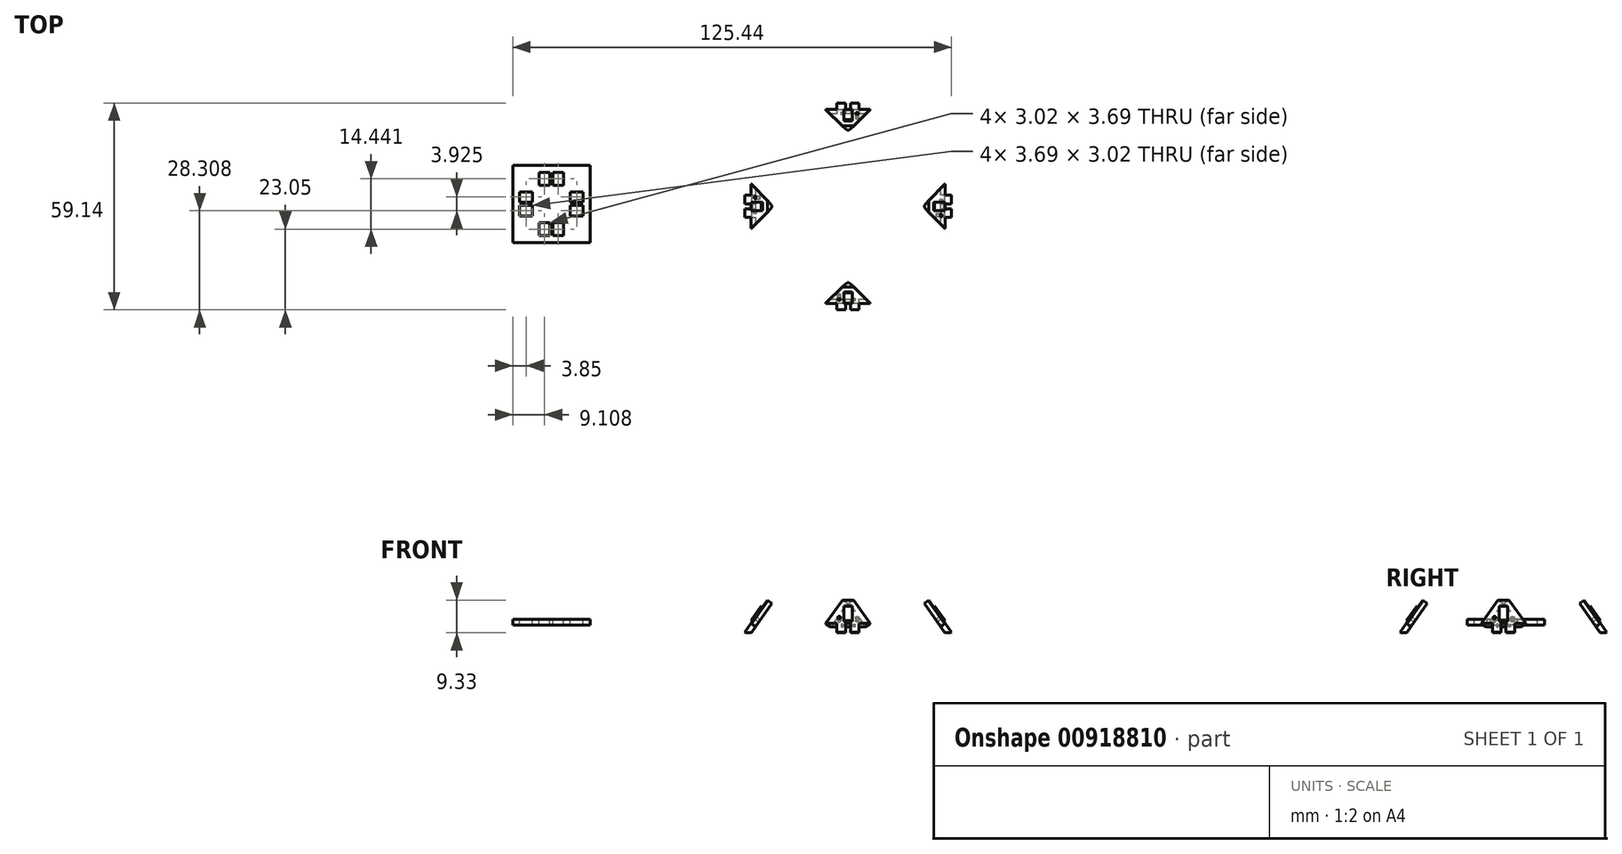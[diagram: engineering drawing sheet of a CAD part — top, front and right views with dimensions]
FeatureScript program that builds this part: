
annotation { "Feature Type Name" : "Feature", "Feature Type Description" : "" }
export const myFeature = defineFeature(function(context is Context, id is Id, definition is map)
    precondition{}
    {
        {
            var Q0;
            Q0=qCreatedBy(makeId("Top.planeOp"),FACE);
            var sketch = newSketch(context, id + "F0", { "sketchPlane" : qUnion([Q0])});
            skLineSegment(sketch, "E0", {"start": v(0, 0) * mm, "end": v(0, 27.35) * mm});
            skLineSegment(sketch, "E1", {"start": v(0, 0) * mm, "end": v(10, 0) * mm});
            skLineSegment(sketch, "E2", {"start": v(10, 0) * mm, "end": v(10, -10) * mm});
            skLineSegment(sketch, "E3", {"start": v(10, -10) * mm, "end": v(0, 0) * mm});
            skLineSegment(sketch, "E4", {"start": v(-60.25, -8.37) * mm, "end": v(-60.25, -4.67) * mm});
            skLineSegment(sketch, "E5", {"start": v(-63.27, -8.37) * mm, "end": v(-63.27, -4.97) * mm});
            skLineSegment(sketch, "E6", {"start": v(-63.27, -4.97) * mm, "end": v(-63.27, -4.67) * mm});
            skLineSegment(sketch, "E7", {"start": v(-63.27, -4.67) * mm, "end": v(-60.25, -4.67) * mm});
            skLineSegment(sketch, "E8", {"start": v(-63.27, -8.37) * mm, "end": v(-60.25, -8.37) * mm});
            skLineSegment(sketch, "E9", {"start": v(-63.27, -8.37) * mm, "end": v(-63.27, -8.07) * mm});
            skLineSegment(sketch, "E10", {"start": v(-59.35, -8.37) * mm, "end": v(-59.35, -4.67) * mm});
            skLineSegment(sketch, "E11", {"start": v(-56.33, -8.37) * mm, "end": v(-56.33, -4.97) * mm});
            skLineSegment(sketch, "E12", {"start": v(-56.33, -4.97) * mm, "end": v(-56.33, -4.67) * mm});
            skLineSegment(sketch, "E13", {"start": v(-56.33, -4.67) * mm, "end": v(-59.35, -4.67) * mm});
            skLineSegment(sketch, "E14", {"start": v(-56.33, -8.37) * mm, "end": v(-59.35, -8.37) * mm});
            skLineSegment(sketch, "E15", {"start": v(-56.33, -8.37) * mm, "end": v(-56.33, -8.07) * mm});
            skLineSegment(sketch, "E16", {"start": v(-50.73, 1.15) * mm, "end": v(-54.43, 1.15) * mm});
            skLineSegment(sketch, "E17", {"start": v(-50.73, 4.17) * mm, "end": v(-54.13, 4.17) * mm});
            skLineSegment(sketch, "E18", {"start": v(-54.13, 4.17) * mm, "end": v(-54.43, 4.17) * mm});
            skLineSegment(sketch, "E19", {"start": v(-54.43, 4.17) * mm, "end": v(-54.43, 1.15) * mm});
            skLineSegment(sketch, "E20", {"start": v(-50.73, 4.17) * mm, "end": v(-50.73, 1.15) * mm});
            skLineSegment(sketch, "E21", {"start": v(-50.73, 4.17) * mm, "end": v(-51.03, 4.17) * mm});
            skLineSegment(sketch, "E22", {"start": v(-50.73, 0.25) * mm, "end": v(-54.43, 0.25) * mm});
            skLineSegment(sketch, "E23", {"start": v(-50.73, -2.77) * mm, "end": v(-54.13, -2.77) * mm});
            skLineSegment(sketch, "E24", {"start": v(-54.13, -2.77) * mm, "end": v(-54.43, -2.77) * mm});
            skLineSegment(sketch, "E25", {"start": v(-54.43, -2.77) * mm, "end": v(-54.43, 0.25) * mm});
            skLineSegment(sketch, "E26", {"start": v(-50.73, -2.77) * mm, "end": v(-50.73, 0.25) * mm});
            skLineSegment(sketch, "E27", {"start": v(-50.73, -2.77) * mm, "end": v(-51.03, -2.77) * mm});
            skLineSegment(sketch, "E28", {"start": v(-60.25, 9.77) * mm, "end": v(-60.25, 6.07) * mm});
            skLineSegment(sketch, "E29", {"start": v(-63.27, 9.77) * mm, "end": v(-63.27, 6.37) * mm});
            skLineSegment(sketch, "E30", {"start": v(-63.27, 6.37) * mm, "end": v(-63.27, 6.07) * mm});
            skLineSegment(sketch, "E31", {"start": v(-63.27, 6.07) * mm, "end": v(-60.25, 6.07) * mm});
            skLineSegment(sketch, "E32", {"start": v(-63.27, 9.77) * mm, "end": v(-60.25, 9.77) * mm});
            skLineSegment(sketch, "E33", {"start": v(-63.27, 9.77) * mm, "end": v(-63.27, 9.47) * mm});
            skLineSegment(sketch, "E34", {"start": v(-59.35, 9.77) * mm, "end": v(-59.35, 6.07) * mm});
            skLineSegment(sketch, "E35", {"start": v(-56.33, 9.77) * mm, "end": v(-56.33, 6.37) * mm});
            skLineSegment(sketch, "E36", {"start": v(-56.33, 6.37) * mm, "end": v(-56.33, 6.07) * mm});
            skLineSegment(sketch, "E37", {"start": v(-56.33, 6.07) * mm, "end": v(-59.35, 6.07) * mm});
            skLineSegment(sketch, "E38", {"start": v(-56.33, 9.77) * mm, "end": v(-59.35, 9.77) * mm});
            skLineSegment(sketch, "E39", {"start": v(-56.33, 9.77) * mm, "end": v(-56.33, 9.47) * mm});
            skLineSegment(sketch, "E40", {"start": v(-68.87, 1.15) * mm, "end": v(-65.17, 1.15) * mm});
            skLineSegment(sketch, "E41", {"start": v(-68.87, 4.17) * mm, "end": v(-65.47, 4.17) * mm});
            skLineSegment(sketch, "E42", {"start": v(-65.47, 4.17) * mm, "end": v(-65.17, 4.17) * mm});
            skLineSegment(sketch, "E43", {"start": v(-65.17, 4.17) * mm, "end": v(-65.17, 1.15) * mm});
            skLineSegment(sketch, "E44", {"start": v(-68.87, 4.17) * mm, "end": v(-68.87, 1.15) * mm});
            skLineSegment(sketch, "E45", {"start": v(-68.87, 4.17) * mm, "end": v(-68.57, 4.17) * mm});
            skLineSegment(sketch, "E46", {"start": v(-68.87, 0.25) * mm, "end": v(-65.17, 0.25) * mm});
            skLineSegment(sketch, "E47", {"start": v(-68.87, -2.77) * mm, "end": v(-65.47, -2.77) * mm});
            skLineSegment(sketch, "E48", {"start": v(-65.47, -2.77) * mm, "end": v(-65.17, -2.77) * mm});
            skLineSegment(sketch, "E49", {"start": v(-65.17, -2.77) * mm, "end": v(-65.17, 0.25) * mm});
            skLineSegment(sketch, "E50", {"start": v(-68.87, -2.77) * mm, "end": v(-68.87, 0.25) * mm});
            skLineSegment(sketch, "E51", {"start": v(-68.87, -2.77) * mm, "end": v(-68.57, -2.77) * mm});
            skLineSegment(sketch, "E52", {"start": v(-48.73, 0.7) * mm, "end": v(-48.73, -10.37) * mm});
            skLineSegment(sketch, "E53", {"start": v(-48.73, -10.37) * mm, "end": v(-59.8, -10.37) * mm});
            skLineSegment(sketch, "E54", {"start": v(-70.87, 0.7) * mm, "end": v(-70.87, -10.37) * mm});
            skLineSegment(sketch, "E55", {"start": v(-70.87, -10.37) * mm, "end": v(-59.8, -10.37) * mm});
            skLineSegment(sketch, "E56", {"start": v(-48.73, 0.7) * mm, "end": v(-48.73, 11.77) * mm});
            skLineSegment(sketch, "E57", {"start": v(-48.73, 11.77) * mm, "end": v(-59.8, 11.77) * mm});
            skLineSegment(sketch, "E58", {"start": v(-70.87, 0.7) * mm, "end": v(-70.87, 11.77) * mm});
            skLineSegment(sketch, "E59", {"start": v(-70.87, 11.77) * mm, "end": v(-59.8, 11.77) * mm});
            skSolve(sketch);
        }
        {
            var Q0;
            Q0=sQuery(id+"F0.wireOp",EDGE,"E0");
            cPlane(context, id + "F1", {"entities" : qUnion([Q0]), "cplaneType" : CPlaneType.LINE_ANGLE, "offset" : 25 * mm, "angle" : 54.74 * degree, "oppositeDirection" : true, "width" : 150 * mm, "height" : 150 * mm});
        }
        {
            var Q0;
            Q0=qCreatedBy(id+"F1.planeOp",FACE);
            var sketch = newSketch(context, id + "F2", { "sketchPlane" : qUnion([Q0])});
            skLineSegment(sketch, "E60", {"start": v(6.35, -2.55) * mm, "end": v(1.62, 5.64) * mm});
            skLineSegment(sketch, "E61", {"start": v(-1.62, 5.64) * mm, "end": v(-6.35, -2.55) * mm});
            skLineSegment(sketch, "E62", {"start": v(3.18, -5.64) * mm, "end": v(0.75, -5.64) * mm});
            skLineSegment(sketch, "E63", {"start": v(-0.75, -5.64) * mm, "end": v(-3.18, -5.64) * mm});
            skLineSegment(sketch, "E64", {"start": v(1.62, 5.64) * mm, "end": v(-1.62, 5.64) * mm});
            skLineSegment(sketch, "E65", {"start": v(-3.18, -5.64) * mm, "end": v(-3.18, -2.55) * mm});
            skLineSegment(sketch, "E66", {"start": v(3.18, -5.64) * mm, "end": v(3.18, -2.55) * mm});
            skLineSegment(sketch, "E67", {"start": v(-6.35, -2.55) * mm, "end": v(-3.18, -2.55) * mm});
            skLineSegment(sketch, "E68", {"start": v(3.18, -2.55) * mm, "end": v(6.35, -2.55) * mm});
            skLineSegment(sketch, "E69", {"start": v(-0.75, -5.64) * mm, "end": v(-0.75, -2.55) * mm});
            skCircle(sketch, "E70", {"center": v(-2.55, -0.48) * mm, "radius": 0.42 * mm});
            skLineSegment(sketch, "E71", {"start": v(-0.75, -2.55) * mm, "end": v(0.75, -2.55) * mm});
            skLineSegment(sketch, "E72", {"start": v(0.75, -2.55) * mm, "end": v(0.75, -5.64) * mm});
            skLineSegment(sketch, "E73", {"start": v(1.96, -2.55) * mm, "end": v(1.46, -2.55) * mm});
            skLineSegment(sketch, "E74", {"start": v(1.46, -2.55) * mm, "end": v(1.46, -2.05) * mm});
            skLineSegment(sketch, "E75", {"start": v(1.46, -2.05) * mm, "end": v(1.96, -2.05) * mm});
            skLineSegment(sketch, "E76", {"start": v(1.96, -2.05) * mm, "end": v(1.96, -2.55) * mm});
            skSolve(sketch);
        }
        {
            var Q0;
            Q0=qSketchRegion(id+"F2",true);
            var Q1;
            Q1=makeQuery(id+"F2.imprint","IMPRINT",FACE,{"disambiguationData":[TD([[makeQuery(id+"F2.imprint","IMPRINT",EDGE,{"derivedFrom":sQuery(id+"F2.wireOp",EDGE,"E73")}),-1.0]])]});
            extrude(context, id + "F3", {"entities" : qUnion([Q0, Q1]), "depth" : 1.6 * mm, "offsetDistance" : 25 * mm});
        }
        {
            var Q0;
            Q0=makeQuery(id+"F2.imprint","IMPRINT",FACE,{"disambiguationData":[TD([[makeQuery(id+"F2.imprint","IMPRINT",EDGE,{"derivedFrom":sQuery(id+"F2.wireOp",EDGE,"E73")}),-1.0]])]});
            extrude(context, id + "F4", {"entities" : qUnion([Q0]), "operationType" : NewBodyOperationType.REMOVE, "depth" : .6 * mm, "offsetDistance" : 25 * mm});
        }
        {
            var Q0;
            Q0=qCreatedBy(makeId("Right.planeOp"),FACE);
            cPlane(context, id + "F5", {"entities" : qUnion([Q0]), "cplaneType" : CPlaneType.OFFSET, "offset" : 25 * mm, "width" : 150 * mm, "height" : 150 * mm});
        }
        {
            var Q0;
            Q0=qCreatedBy(id+"F5.planeOp",FACE);
            var sketch = newSketch(context, id + "F6", { "sketchPlane" : qUnion([Q0])});
            skLineSegment(sketch, "E77", {"start": v(0, 0) * mm, "end": v(0, 26.14) * mm});
            skSolve(sketch);
        }
        {
            var Q0;
            Q0=qCreatedBy(makeId("Front.planeOp"),FACE);
            var sketch = newSketch(context, id + "F7", { "sketchPlane" : qUnion([Q0])});
            skPoint(sketch, "E78.0", {"position": v(-4.57, -3.69) * mm});
            skPoint(sketch, "E78.1", {"position": v(-3.26, -4.6) * mm});
            skPoint(sketch, "E78.2", {"position": v(-2.37, -3.35) * mm});
            skLineSegment(sketch, "E79", {"start": v(-3.26, -4.6) * mm, "end": v(-4.57, -3.69) * mm});
            skLineSegment(sketch, "E80", {"start": v(-4.57, -3.69) * mm, "end": v(-4.4, -3.8) * mm});
            skLineSegment(sketch, "E81", {"start": v(-3.26, -4.6) * mm, "end": v(-2.62, -3.71) * mm});
            skLineSegment(sketch, "E82", {"start": v(-2.62, -3.71) * mm, "end": v(-4.4, -3.8) * mm});
            skSolve(sketch);
        }
        {
            var Q0;
            Q0=makeQuery(id+"F7.imprint","IMPRINT",FACE,{"disambiguationData":[TD([[makeQuery(id+"F7.imprint","IMPRINT",EDGE,{"derivedFrom":sQuery(id+"F7.wireOp",EDGE,"E79")}),-1.0]])]});
            extrude(context, id + "F8", {"entities" : qUnion([Q0]), "operationType" : NewBodyOperationType.REMOVE, "endBound" : BoundingType.SYMMETRIC, "oppositeDirection" : true, "depth" : 25 * mm, "offsetDistance" : 25 * mm});
        }
        {
            var Q0;
            Q0=makeQuery(id+"F3.opExtrude","SWEPT_FACE",FACE,{"disambiguationData":[OSD([sQuery(id+"F2.wireOp",EDGE,"E64")])]});
            var sketch = newSketch(context, id + "F9", { "sketchPlane" : qUnion([Q0])});
            skPoint(sketch, "E83.0", {"position": v(0, -1.62) * mm});
            skPoint(sketch, "E83.1", {"position": v(-1.6, -1.62) * mm});
            skPoint(sketch, "E83.2", {"position": v(0, 1.62) * mm});
            skPoint(sketch, "E83.3", {"position": v(-1.6, 1.62) * mm});
            skLineSegment(sketch, "E84", {"start": v(0, -1.62) * mm, "end": v(0, -0.22) * mm});
            skLineSegment(sketch, "E85", {"start": v(0, -1.62) * mm, "end": v(-1.4, -1.62) * mm});
            skLineSegment(sketch, "E86", {"start": v(0, 1.62) * mm, "end": v(0, 0.22) * mm});
            skLineSegment(sketch, "E87", {"start": v(0, 1.62) * mm, "end": v(-1.4, 1.62) * mm});
            skLineSegment(sketch, "E88", {"start": v(-1.4, 1.62) * mm, "end": v(0, 0.22) * mm});
            skLineSegment(sketch, "E89", {"start": v(0, -0.22) * mm, "end": v(-1.4, -1.62) * mm});
            skSolve(sketch);
        }
        {
            var Q0;
            Q0=makeQuery(id+"F9.imprint","IMPRINT",FACE,{"disambiguationData":[TD([[makeQuery(id+"F9.imprint","IMPRINT",EDGE,{"derivedFrom":sQuery(id+"F9.wireOp",EDGE,"E86")}),1.0]])]});
            var Q1;
            Q1=sQuery(id+"F2.wireOp",EDGE,"E61");
            sweep(context, id + "F10", {"operationType" : NewBodyOperationType.REMOVE, "profiles" : qUnion([Q0]), "path" : qUnion([Q1])});
        }
        {
            var Q0;
            Q0=makeQuery(id+"F9.imprint","IMPRINT",FACE,{"disambiguationData":[TD([[makeQuery(id+"F9.imprint","IMPRINT",EDGE,{"derivedFrom":sQuery(id+"F9.wireOp",EDGE,"E84")}),1.0]])]});
            var Q1;
            Q1=sQuery(id+"F2.wireOp",EDGE,"E60");
            sweep(context, id + "F11", {"operationType" : NewBodyOperationType.REMOVE, "profiles" : qUnion([Q0]), "path" : qUnion([Q1])});
        }
        {
            var Q0;
            Q0=makeQuery(id+"F3.opExtrude","CAP_FACE",FACE,{"disambiguationData":[OSD([sQuery(id+"F2.wireOp",EDGE,"E60"),sQuery(id+"F2.wireOp",EDGE,"E61"),sQuery(id+"F2.wireOp",EDGE,"E62"),sQuery(id+"F2.wireOp",EDGE,"E63"),sQuery(id+"F2.wireOp",EDGE,"E64"),sQuery(id+"F2.wireOp",EDGE,"E65"),sQuery(id+"F2.wireOp",EDGE,"E66"),sQuery(id+"F2.wireOp",EDGE,"E67"),sQuery(id+"F2.wireOp",EDGE,"E68"),sQuery(id+"F2.wireOp",EDGE,"E69"),sQuery(id+"F2.wireOp",EDGE,"E70"),sQuery(id+"F2.wireOp",EDGE,"E71"),sQuery(id+"F2.wireOp",EDGE,"E72")])],"isStart":false});
            var sketch = newSketch(context, id + "F12", { "sketchPlane" : qUnion([Q0])});
            skPoint(sketch, "E90.0", {"position": v(0, -2.55) * mm});
            skLineSegment(sketch, "E91", {"start": v(0, -2.55) * mm, "end": v(0, -2.55) * mm});
            skLineSegment(sketch, "E92", {"start": v(0, -2.55) * mm, "end": v(0, -1.86) * mm});
            skLineSegment(sketch, "E93", {"start": v(0, -1.86) * mm, "end": v(1.25, -1.86) * mm});
            skLineSegment(sketch, "E94", {"start": v(1.25, -1.86) * mm, "end": v(1.25, 3.24) * mm});
            skLineSegment(sketch, "E95", {"start": v(1.25, 3.24) * mm, "end": v(-1.25, 3.24) * mm});
            skLineSegment(sketch, "E96", {"start": v(-1.25, 3.24) * mm, "end": v(-1.25, -1.86) * mm});
            skLineSegment(sketch, "E97", {"start": v(-1.25, -1.86) * mm, "end": v(0, -1.86) * mm});
            skSolve(sketch);
        }
        {
            var Q0;
            Q0=makeQuery(id+"F12.imprint","IMPRINT",FACE,{"disambiguationData":[TD([[makeQuery(id+"F12.imprint","IMPRINT",EDGE,{"derivedFrom":sQuery(id+"F12.wireOp",EDGE,"E93")}),1.0]])]});
            extrude(context, id + "F13", {"entities" : qUnion([Q0]), "operationType" : NewBodyOperationType.ADD, "depth" : 0.4 * mm, "offsetDistance" : 25 * mm});
        }
        {
            var Q0;
            Q0=makeQuery(id+"F3.opExtrude","SWEPT_BODY",BODY,{"disambiguationData":[OSD([sQuery(id+"F2.wireOp",EDGE,"E60"),sQuery(id+"F2.wireOp",EDGE,"E61"),sQuery(id+"F2.wireOp",EDGE,"E62"),sQuery(id+"F2.wireOp",EDGE,"E63"),sQuery(id+"F2.wireOp",EDGE,"E64"),sQuery(id+"F2.wireOp",EDGE,"E65"),sQuery(id+"F2.wireOp",EDGE,"E66"),sQuery(id+"F2.wireOp",EDGE,"E67"),sQuery(id+"F2.wireOp",EDGE,"E68"),sQuery(id+"F2.wireOp",EDGE,"E69"),sQuery(id+"F2.wireOp",EDGE,"E70"),sQuery(id+"F2.wireOp",EDGE,"E71"),sQuery(id+"F2.wireOp",EDGE,"E72")])]});
            var Q1;
            Q1=sQuery(id+"F6.wireOp",EDGE,"E77");
            circularPattern(context, id + "F14", {"entities" : qUnion([Q0]), "axis" : qUnion([Q1]), "angle" : 360 * degree, "instanceCount" : 4, "equalSpace" : true});
        }
        {
            var Q0;
            Q0=makeQuery(id+"F0.imprint","IMPRINT",FACE,{"disambiguationData":[TD([[makeQuery(id+"F0.imprint","IMPRINT",EDGE,{"derivedFrom":sQuery(id+"F0.wireOp",EDGE,"E4")}),-1.0]])]});
            extrude(context, id + "F15", {"entities" : qUnion([Q0]), "oppositeDirection" : true, "depth" : 1.6 * mm, "offsetDistance" : 25 * mm});
        }
    });
